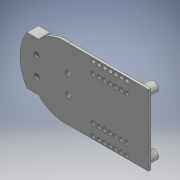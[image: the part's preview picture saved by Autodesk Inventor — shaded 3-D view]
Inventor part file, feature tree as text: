
AUTODESK INVENTOR PART (.ipt)
format: ipt  version: 2016 (Build 200138000, 138)  size: 221,696 bytes
history: native  units: mm
features: sketch x5, hole x3, extrude x2, projected_geometry x1
ambient origin geometry x8: Origin, YZ Plane, XZ Plane, XY Plane, X Axis, Y Axis, Z Axis, Center Point
bodies: Solid1 (feature_tree)
feature tree (11):
  extrude  "Extrusion1"  Depth=76.0mm
  extrude  "Extrusion2"  Depth=10.0mm
  hole  "Hole1"  [1 undecoded]
  hole  "Hole2"  [1 undecoded]
  hole  "Hole3"  [1 undecoded]
  sketch  "Sketch1"  dims[d1=86.0mm d2=76.0mm]
  sketch  "Sketch2"  dims[d3=10.0mm d4=10.0mm]
  sketch  "Sketch4"  dims[d6=12.0mm d7=12.0mm]
  sketch  "Sketch5"  dims[d8=2.4mm d9=0.0mm d10=10.0mm]
  projected_geometry  "Projected Loop1"
  sketch  "Sketch6"  dims[d11=10.0mm d12=63.0mm d13=6.5mm d14=6.5mm d15=6.5mm d16=10.0mm d17=0.0mm d20=6.5mm d21=6.5mm d22=127.167mm d23=6.5mm d24=6.5mm d25=6.0mm d26=4.0mm d27=2.0mm d28=90.0deg d29=9.0mm d30=0.0mm d36=5.5mm d38=5.5mm d39=10.0mm d40=10.0mm d41=5.5mm d42=5.5mm d43=34.0mm d44=34.0mm d45=5.5mm d46=6.0mm d47=4.0mm d48=2.0mm d49=90.0deg d50=9.0mm d51=0.0mm d52=27.0mm d54=4.4mm d57=4.4mm d59=4.4mm d61=4.4mm d63=4.4mm d64=6.0mm d65=4.0mm d66=2.0mm d67=90.0deg d68=9.0mm d69=0.0mm d70=63.0mm d71=23.0mm d73=23.0mm d74=23.0mm d75=23.0mm d76=12.0mm d77=4.4mm d78=4.4mm d79=4.4mm d80=6.0mm d81=4.4mm d82=6.0mm d83=4.4mm d84=6.0mm]
note: 3 required parameter values undecoded (feature->parameter linkage not recoverable at this tier; creation-order binding heuristic only, values carry confidence <= 0.55)
